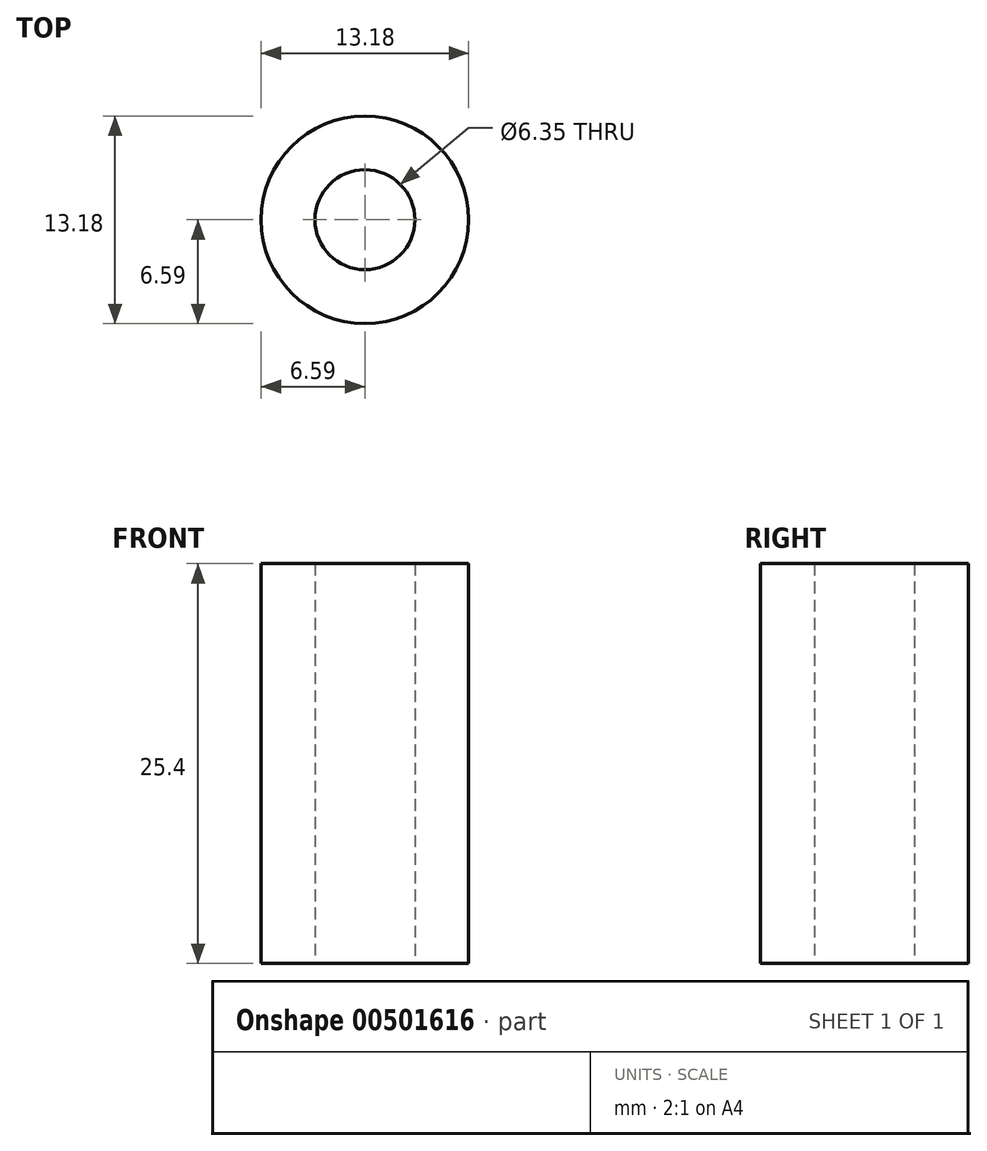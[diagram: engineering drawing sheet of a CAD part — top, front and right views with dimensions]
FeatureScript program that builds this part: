
annotation { "Feature Type Name" : "Feature", "Feature Type Description" : "" }
export const myFeature = defineFeature(function(context is Context, id is Id, definition is map)
    precondition{}
    {
        {
            var Q0;
            Q0=qCreatedBy(makeId("Top.planeOp"),FACE);
            var sketch = newSketch(context, id + "F0", { "sketchPlane" : qUnion([Q0])});
            skCircle(sketch, "E0", {"center": v(0, 0) * mm, "radius": 3.18 * mm});
            skCircle(sketch, "E1", {"center": v(0, 0) * mm, "radius": 6.59 * mm});
            skSolve(sketch);
        }
        {
            var Q0;
            Q0=qSketchRegion(id+"F0",true);
            extrude(context, id + "F1", {"entities" : qUnion([Q0]), "depth" : 25.4 * mm});
        }
    });
